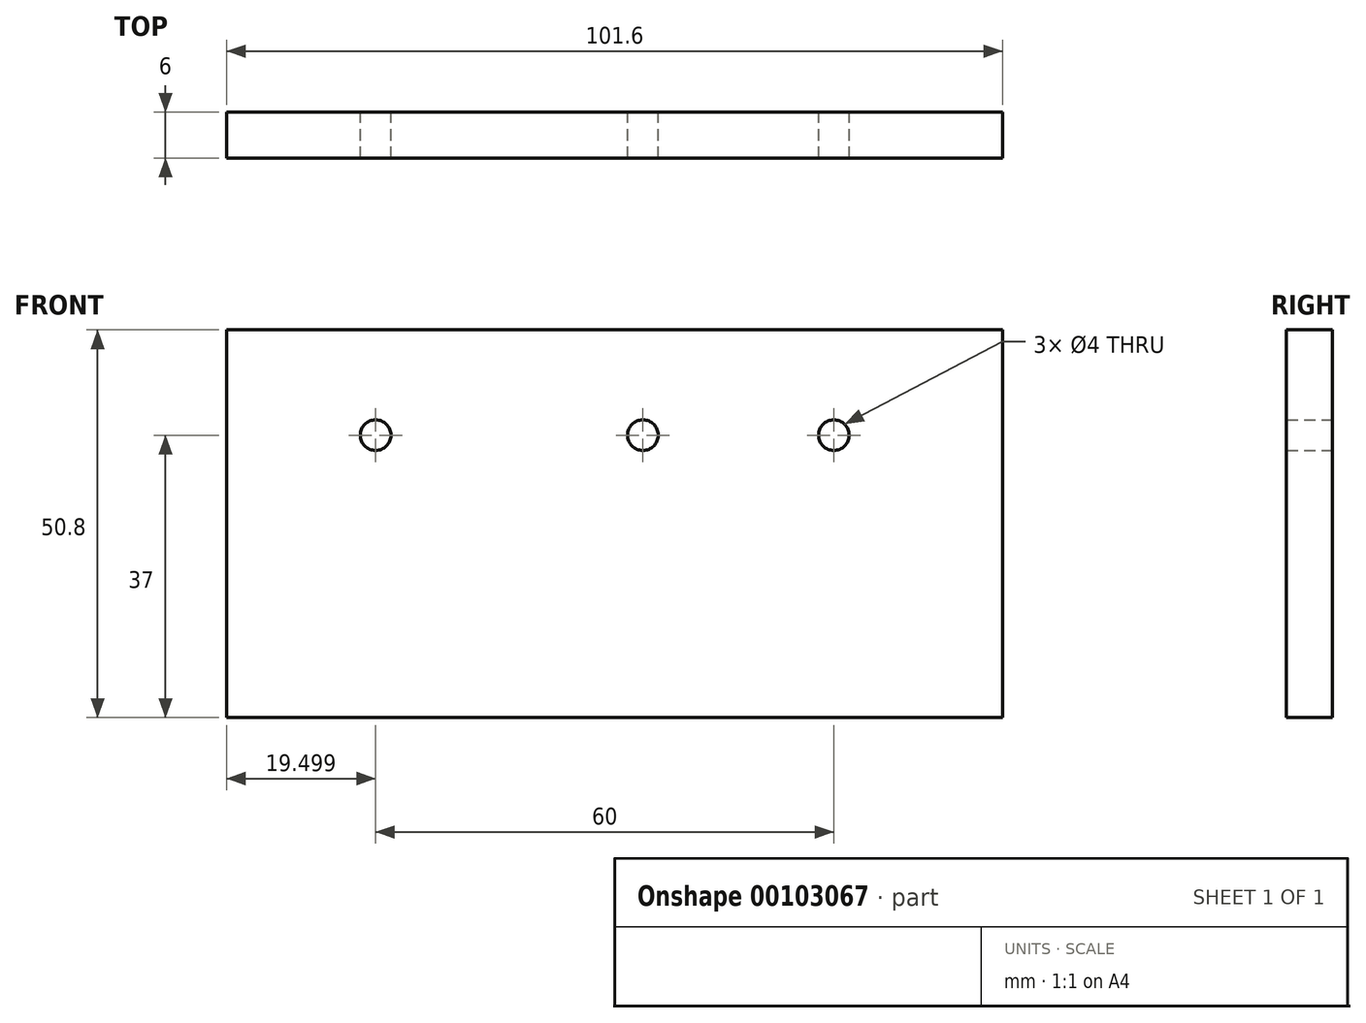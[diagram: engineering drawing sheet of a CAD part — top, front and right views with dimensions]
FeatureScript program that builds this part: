
annotation { "Feature Type Name" : "Feature", "Feature Type Description" : "" }
export const myFeature = defineFeature(function(context is Context, id is Id, definition is map)
    precondition{}
    {
        {
            var Q0;
            Q0=qCreatedBy(makeId("Front.planeOp"),FACE);
            var sketch = newSketch(context, id + "F0", { "sketchPlane" : qUnion([Q0])});
            skLineSegment(sketch, "E0.bottom", {"start": v(-95.88, 13.8) * mm, "end": v(5.72, 13.8) * mm});
            skLineSegment(sketch, "E0.top", {"start": v(-95.88, -37) * mm, "end": v(5.72, -37) * mm});
            skLineSegment(sketch, "E0.left", {"start": v(-95.88, 13.8) * mm, "end": v(-95.88, -37) * mm});
            skLineSegment(sketch, "E0.right", {"start": v(5.72, 13.8) * mm, "end": v(5.72, -37) * mm});
            skCircle(sketch, "E1", {"center": v(-76.38, 0) * mm, "radius": 2 * mm});
            skCircle(sketch, "E2", {"center": v(-41.38, 0) * mm, "radius": 2 * mm});
            skCircle(sketch, "E3", {"center": v(-16.38, 0) * mm, "radius": 2 * mm});
            skSolve(sketch);
        }
        {
            var Q0;
            Q0=makeQuery(id+"F0.imprint","IMPRINT",FACE,{"disambiguationData":[TD([[makeQuery(id+"F0.imprint","IMPRINT",EDGE,{"derivedFrom":sQuery(id+"F0.wireOp",EDGE,"E0.bottom")}),-1.0]])]});
            extrude(context, id + "F1", {"entities" : qUnion([Q0]), "depth" : 6 * mm});
        }
    });
